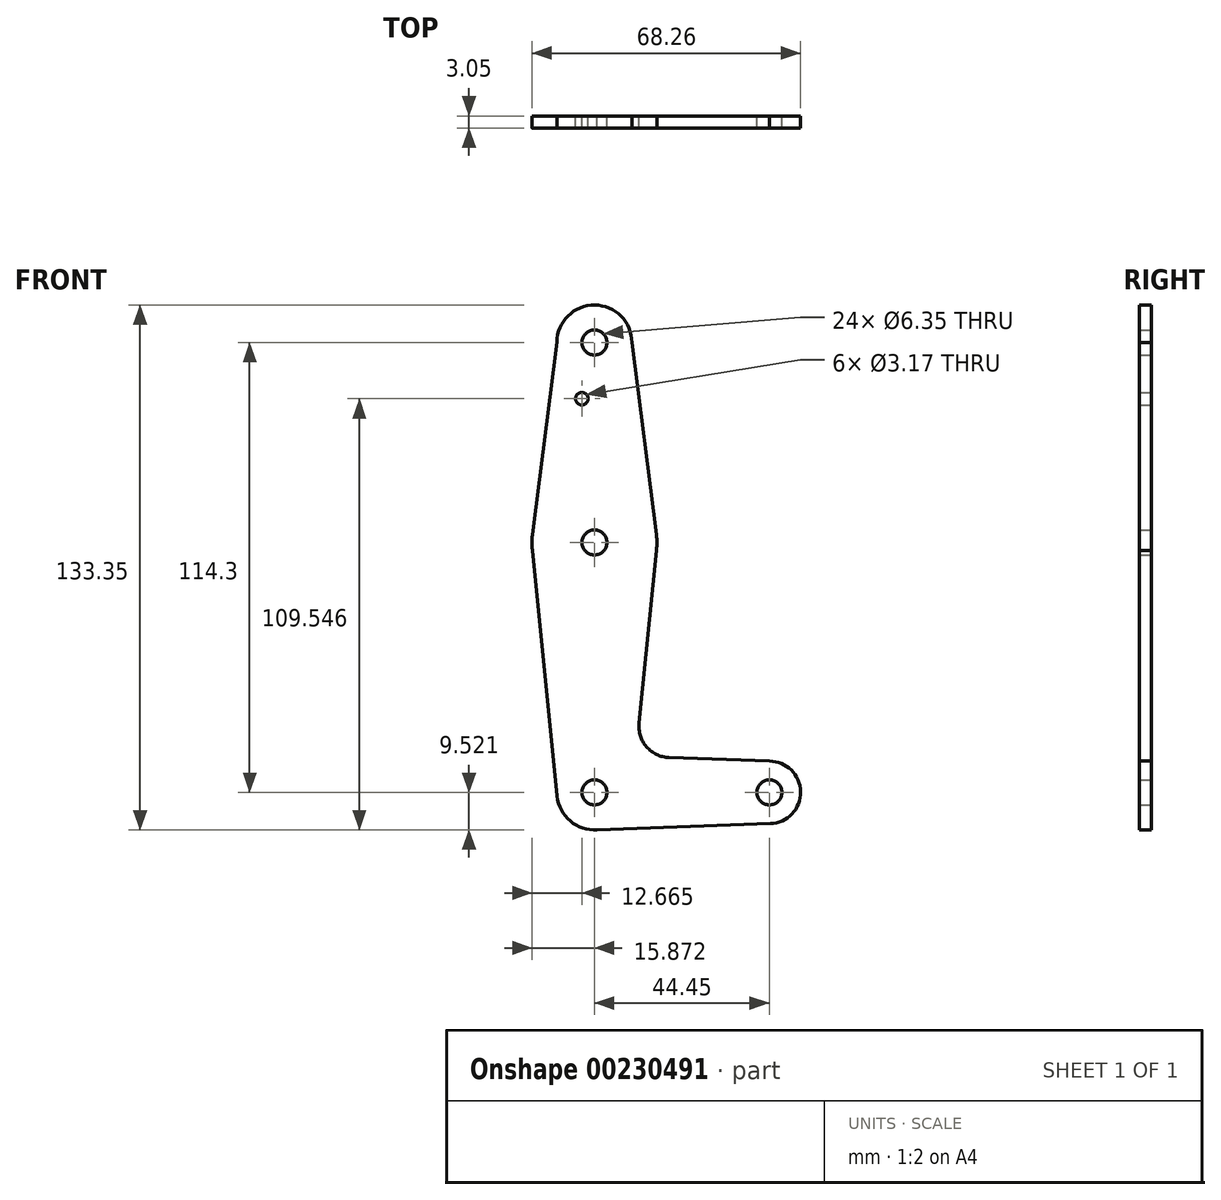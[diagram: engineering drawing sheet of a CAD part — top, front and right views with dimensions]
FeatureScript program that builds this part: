
annotation { "Feature Type Name" : "Feature", "Feature Type Description" : "" }
export const myFeature = defineFeature(function(context is Context, id is Id, definition is map)
    precondition{}
    {
        {
            var Q0;
            Q0=qCreatedBy(makeId("Front.planeOp"),FACE);
            var sketch = newSketch(context, id + "F0", { "sketchPlane" : qUnion([Q0])});
            skLineSegment(sketch, "E0", {"start": v(-17.3, 52.65) * mm, "end": v(-17.3, -61.65) * mm, "construction": true});
            skLineSegment(sketch, "E1", {"start": v(-17.3, -61.65) * mm, "end": v(27.14, -61.65) * mm, "construction": true});
            skCircle(sketch, "E2", {"center": v(-17.3, 52.65) * mm, "radius": 9.53 * mm});
            skCircle(sketch, "E3", {"center": v(-17.3, 1.85) * mm, "radius": 15.88 * mm});
            skCircle(sketch, "E4", {"center": v(-17.3, -61.65) * mm, "radius": 9.53 * mm});
            skCircle(sketch, "E5", {"center": v(27.14, -61.65) * mm, "radius": 7.94 * mm});
            skLineSegment(sketch, "E6", {"start": v(-17.3, -71.17) * mm, "end": v(27.42, -69.58) * mm});
            skLineSegment(sketch, "E7", {"start": v(27.14, -53.71) * mm, "end": v(1.66, -52.8) * mm});
            skCircle(sketch, "E8", {"center": v(-17.3, 52.65) * mm, "radius": 3.18 * mm});
            skCircle(sketch, "E9", {"center": v(-17.3, 1.85) * mm, "radius": 3.18 * mm});
            skCircle(sketch, "E10", {"center": v(-17.3, -61.65) * mm, "radius": 3.18 * mm});
            skCircle(sketch, "E11", {"center": v(27.14, -61.65) * mm, "radius": 3.18 * mm});
            skLineSegment(sketch, "E12", {"start": v(-26.83, 52.74) * mm, "end": v(-33.06, 3.86) * mm});
            skLineSegment(sketch, "E13", {"start": v(-33.06, -0.15) * mm, "end": v(-26.79, -62.6) * mm});
            skLineSegment(sketch, "E14", {"start": v(-7.78, 52.65) * mm, "end": v(-1.56, 3.86) * mm});
            skLineSegment(sketch, "E15", {"start": v(-1.56, -0.15) * mm, "end": v(-5.97, -44.06) * mm});
            skCircle(sketch, "E16", {"center": v(-20.52, 38.38) * mm, "radius": 1.59 * mm});
            skPoint(sketch, "E17.newPointA", {"position": v(-7.83, -62.6) * mm});
            skArc(sketch, "E17.filletArc", {"start": v(-5.97, -44.06) * mm, "mid": v(-4.05, -50.08) * mm, "end": v(1.66, -52.8) * mm});
            skSolve(sketch);
        }
        {
            var Q0;
            Q0 = qSketchRegion(id + "F0", true);
            extrude(context, id + "F1", {"entities" : qUnion([Q0]), "depth" : 3.05 * mm});
        }
    });
